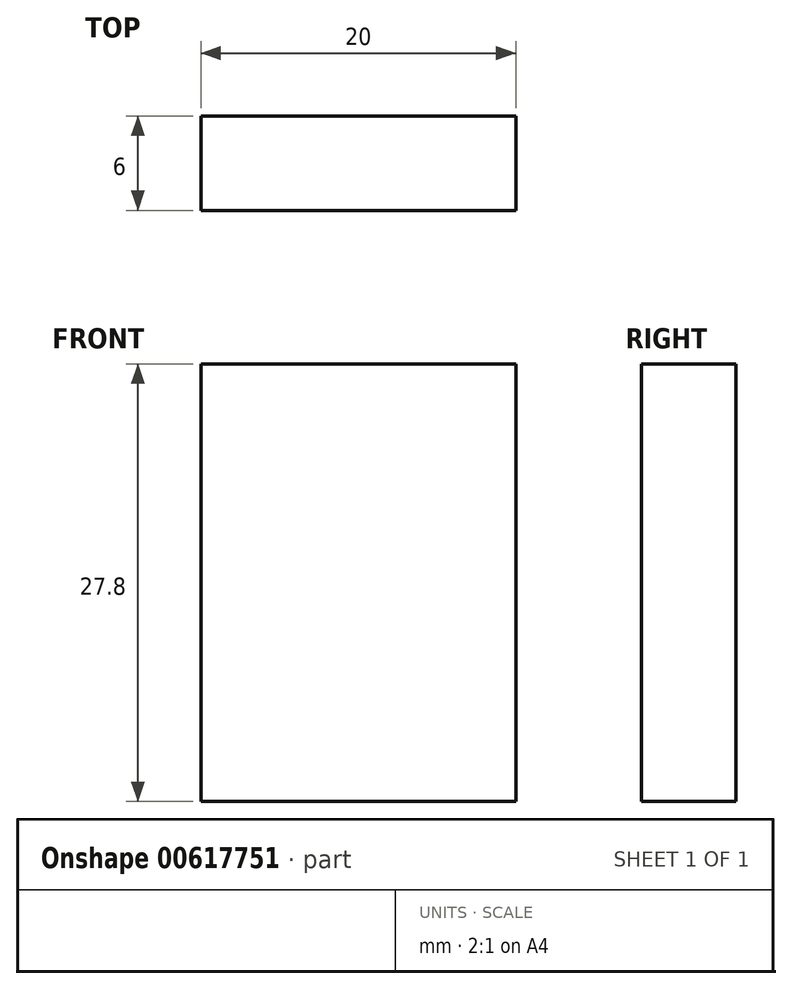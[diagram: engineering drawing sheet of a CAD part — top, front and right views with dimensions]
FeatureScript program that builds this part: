
annotation { "Feature Type Name" : "Feature", "Feature Type Description" : "" }
export const myFeature = defineFeature(function(context is Context, id is Id, definition is map)
    precondition{}
    {
        {
            var Q0;
            Q0=qCreatedBy(makeId("Front.planeOp"),FACE);
            var sketch = newSketch(context, id + "F0", { "sketchPlane" : qUnion([Q0])});
            skLineSegment(sketch, "E0.bottom", {"start": v(-20, 27.8) * mm, "end": v(0, 27.8) * mm});
            skLineSegment(sketch, "E0.top", {"start": v(-20, 0) * mm, "end": v(0, 0) * mm});
            skLineSegment(sketch, "E0.left", {"start": v(-20, 27.8) * mm, "end": v(-20, 0) * mm});
            skLineSegment(sketch, "E0.right", {"start": v(0, 27.8) * mm, "end": v(0, 0) * mm});
            skSolve(sketch);
        }
        {
            var Q0;
            Q0 = qSketchRegion(id + "F0", true);
            extrude(context, id + "F1", {"entities" : qUnion([Q0]), "oppositeDirection" : true, "depth" : 6 * mm, "offsetDistance" : 25 * mm});
        }
    });
